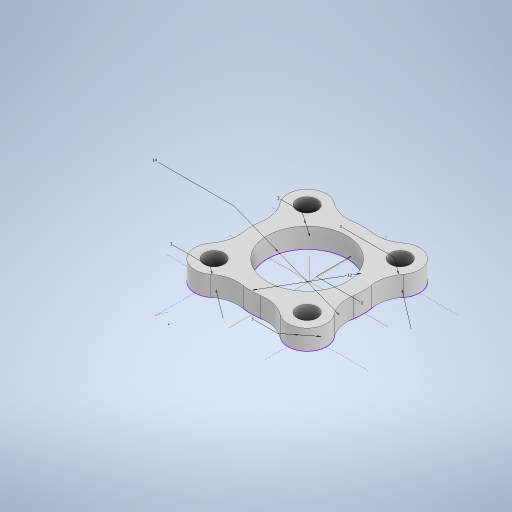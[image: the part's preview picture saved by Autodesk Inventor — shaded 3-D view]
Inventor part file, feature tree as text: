
AUTODESK INVENTOR PART (.ipt)
format: ipt  version: 2024.2 (Build 282272000, 272)  size: 306,688 bytes
history: native  units: mm
features: other x9, extrude x2, sketch x1
ambient origin geometry x8: Origin, YZ Plane, XZ Plane, XY Plane, X Axis, Y Axis, Z Axis, Center Point
bodies: Body1 (feature_tree)
feature tree (12):
  other  "Твердое тело1"
  sketch  "Эскиз1"
  extrude  "Выдавливание1"  Depth=3.0mm TaperAngle=0.0deg
  extrude  "Выдавливание3"  Depth=2.0mm
  other  "Сопряжение грани1"
  other  "Сопряжение грани2"
  other  "Сопряжение грани3"
  other  "Сопряжение грани4"
  other  "Сопряжение грани5"
  other  "Сопряжение грани6"
  other  "Сопряжение грани7"
  other  "Сопряжение грани8"
